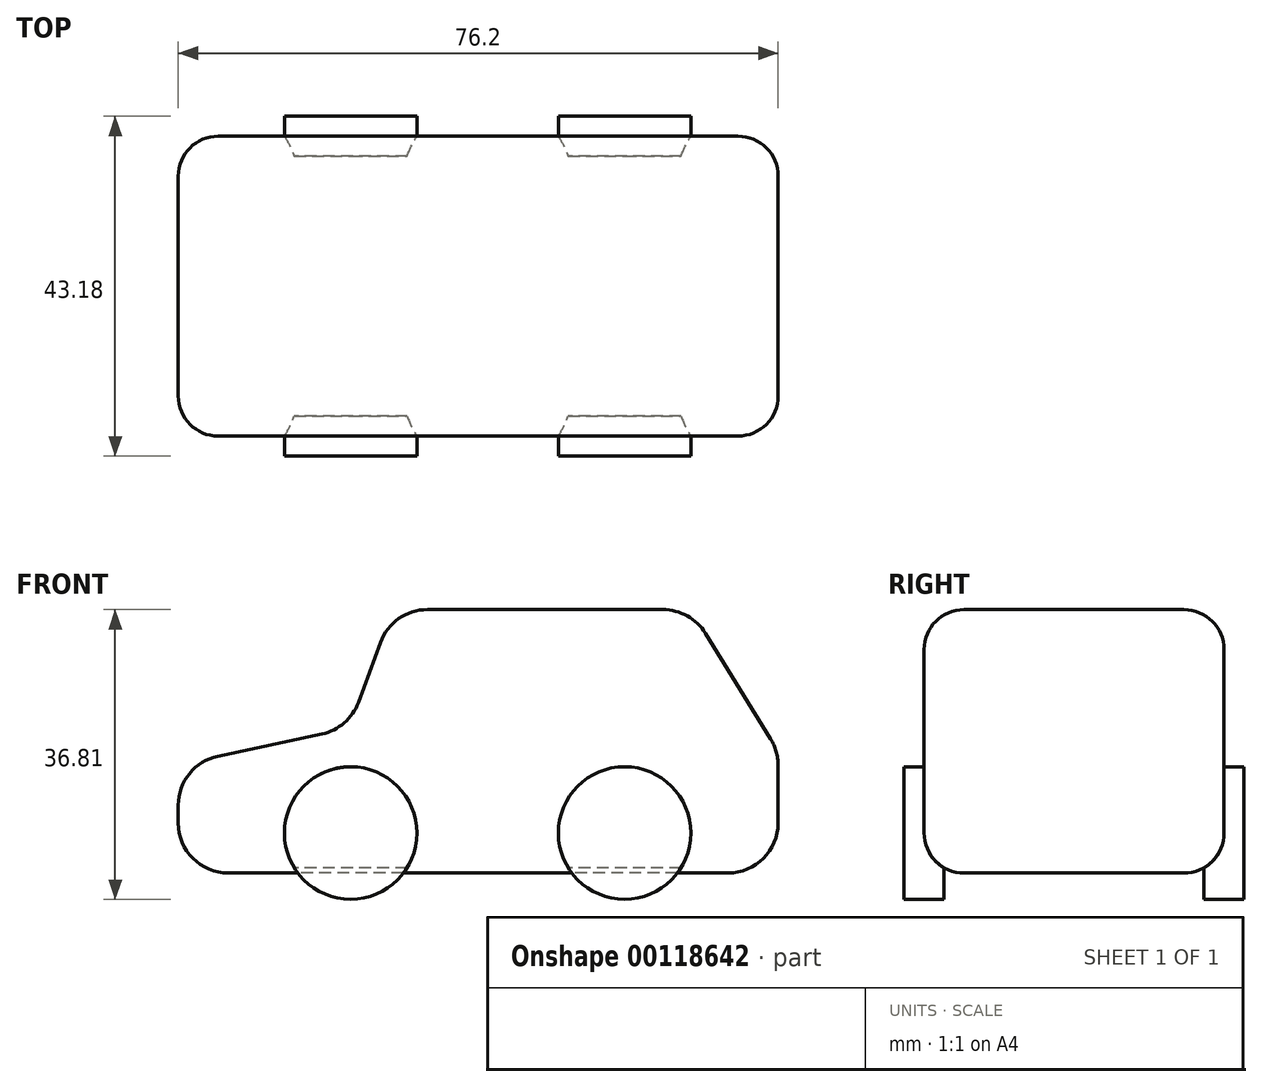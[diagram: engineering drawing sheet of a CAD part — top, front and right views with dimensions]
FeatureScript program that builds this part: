
annotation { "Feature Type Name" : "Feature", "Feature Type Description" : "" }
export const myFeature = defineFeature(function(context is Context, id is Id, definition is map)
    precondition{}
    {
        {
            var Q0;
            Q0=qCreatedBy(makeId("Front.planeOp"),FACE);
            var sketch = newSketch(context, id + "F0", { "sketchPlane" : qUnion([Q0])});
            skLineSegment(sketch, "E0", {"start": v(-45.02, 25.7) * mm, "end": v(-31.8, 28.52) * mm});
            skLineSegment(sketch, "E1", {"start": v(-27.16, 32.54) * mm, "end": v(-24.36, 40.17) * mm});
            skLineSegment(sketch, "E2", {"start": v(-18.4, 44.33) * mm, "end": v(11.53, 44.33) * mm});
            skLineSegment(sketch, "E3", {"start": v(16.93, 41.31) * mm, "end": v(25.2, 27.9) * mm});
            skLineSegment(sketch, "E4", {"start": v(26.15, 24.57) * mm, "end": v(26.15, 17.2) * mm});
            skLineSegment(sketch, "E5", {"start": v(19.8, 10.86) * mm, "end": v(-43.7, 10.86) * mm});
            skLineSegment(sketch, "E6", {"start": v(-50.05, 17.2) * mm, "end": v(-50.05, 19.5) * mm});
            skPoint(sketch, "E7.visualSharp", {"position": v(-28.37, 29.26) * mm});
            skArc(sketch, "E7.filletArc", {"start": v(-31.8, 28.52) * mm, "mid": v(-28.96, 29.94) * mm, "end": v(-27.16, 32.54) * mm});
            skPoint(sketch, "E8.visualSharp", {"position": v(-22.83, 44.33) * mm});
            skArc(sketch, "E8.filletArc", {"start": v(-18.4, 44.33) * mm, "mid": v(-22.03, 43.18) * mm, "end": v(-24.36, 40.17) * mm});
            skPoint(sketch, "E9.visualSharp", {"position": v(15.07, 44.33) * mm});
            skArc(sketch, "E9.filletArc", {"start": v(16.93, 41.31) * mm, "mid": v(14.62, 43.52) * mm, "end": v(11.53, 44.33) * mm});
            skPoint(sketch, "E10.visualSharp", {"position": v(26.15, 26.37) * mm});
            skArc(sketch, "E10.filletArc", {"start": v(26.15, 24.57) * mm, "mid": v(25.91, 26.3) * mm, "end": v(25.2, 27.9) * mm});
            skPoint(sketch, "E11.visualSharp", {"position": v(26.15, 10.86) * mm});
            skArc(sketch, "E11.filletArc", {"start": v(19.8, 10.86) * mm, "mid": v(24.3, 12.72) * mm, "end": v(26.15, 17.2) * mm});
            skPoint(sketch, "E12.visualSharp", {"position": v(-50.05, 10.86) * mm});
            skArc(sketch, "E12.filletArc", {"start": v(-50.05, 17.2) * mm, "mid": v(-48.19, 12.72) * mm, "end": v(-43.7, 10.86) * mm});
            skPoint(sketch, "E13.visualSharp", {"position": v(-50.05, 24.63) * mm});
            skArc(sketch, "E13.filletArc", {"start": v(-45.02, 25.7) * mm, "mid": v(-48.63, 23.48) * mm, "end": v(-50.05, 19.5) * mm});
            skSolve(sketch);
        }
        {
            var Q0;
            Q0 = qSketchRegion(id + "F0", true);
            extrude(context, id + "F1", {"entities" : qUnion([Q0]), "endBound" : BoundingType.SYMMETRIC, "depth" : 38.1 * mm});
        }
        {
            var Q0;
            Q0=makeQuery(id+"F1.opExtrude","CAP_EDGE",EDGE,{"disambiguationData":[OSD([sQuery(id+"F0.wireOp",EDGE,"E2")])],"isStart":false});
            var Q1;
            Q1=makeQuery(id+"F1.opExtrude","CAP_EDGE",EDGE,{"disambiguationData":[OSD([sQuery(id+"F0.wireOp",EDGE,"E2")])],"isStart":true});
            fillet(context, id + "F2", {"entities" : qUnion([Q0, Q1]), "radius" : 5.08 * mm, "tangentPropagation" : true, "allowEdgeOverflow" : false});
        }
        {
            var Q0;
            Q0=makeQuery(id+"F1.opExtrude","CAP_FACE",FACE,{"disambiguationData":[OSD([sQuery(id+"F0.wireOp",EDGE,"E0"),sQuery(id+"F0.wireOp",EDGE,"E1"),sQuery(id+"F0.wireOp",EDGE,"E2"),sQuery(id+"F0.wireOp",EDGE,"E3"),sQuery(id+"F0.wireOp",EDGE,"E4"),sQuery(id+"F0.wireOp",EDGE,"E5"),sQuery(id+"F0.wireOp",EDGE,"E6"),sQuery(id+"F0.wireOp",EDGE,"E7.filletArc"),sQuery(id+"F0.wireOp",EDGE,"E8.filletArc"),sQuery(id+"F0.wireOp",EDGE,"E9.filletArc"),sQuery(id+"F0.wireOp",EDGE,"E10.filletArc"),sQuery(id+"F0.wireOp",EDGE,"E11.filletArc"),sQuery(id+"F0.wireOp",EDGE,"E12.filletArc"),sQuery(id+"F0.wireOp",EDGE,"E13.filletArc")])],"isStart":false});
            var sketch = newSketch(context, id + "F3", { "sketchPlane" : qUnion([Q0])});
            skCircle(sketch, "E14", {"center": v(-28.15, 15.94) * mm, "radius": 8.42 * mm});
            skCircle(sketch, "E15", {"center": v(6.65, 15.94) * mm, "radius": 8.42 * mm});
            skSolve(sketch);
        }
        {
            var Q0;
            {var subQ0=sQuery(id+"F3.wireOp",EDGE,"E15");var subQ1=sQuery(id+"F0.wireOp",EDGE,"E5");var subQ2=makeQuery(id+"F2.opFillet","BLEND_EDGE",EDGE,{"blendedFrom":[makeQuery(id+"F1.opExtrude","CAP_EDGE",EDGE,{"disambiguationData":[OSD([subQ1])],"isStart":false}),makeQuery(id+"F1.opExtrude","CAP_FACE",FACE,{"disambiguationData":[OSD([sQuery(id+"F0.wireOp",EDGE,"E0"),sQuery(id+"F0.wireOp",EDGE,"E1"),sQuery(id+"F0.wireOp",EDGE,"E2"),sQuery(id+"F0.wireOp",EDGE,"E3"),sQuery(id+"F0.wireOp",EDGE,"E4"),subQ1,sQuery(id+"F0.wireOp",EDGE,"E6"),sQuery(id+"F0.wireOp",EDGE,"E7.filletArc"),sQuery(id+"F0.wireOp",EDGE,"E8.filletArc"),sQuery(id+"F0.wireOp",EDGE,"E9.filletArc"),sQuery(id+"F0.wireOp",EDGE,"E10.filletArc"),sQuery(id+"F0.wireOp",EDGE,"E11.filletArc"),sQuery(id+"F0.wireOp",EDGE,"E12.filletArc"),sQuery(id+"F0.wireOp",EDGE,"E13.filletArc")])],"isStart":false})],"blendedInto":[makeQuery(id+"F1.opExtrude","CAP_FACE",FACE,{"disambiguationData":[OSD([sQuery(id+"F0.wireOp",EDGE,"E0"),sQuery(id+"F0.wireOp",EDGE,"E1"),sQuery(id+"F0.wireOp",EDGE,"E2"),sQuery(id+"F0.wireOp",EDGE,"E3"),sQuery(id+"F0.wireOp",EDGE,"E4"),subQ1,sQuery(id+"F0.wireOp",EDGE,"E6"),sQuery(id+"F0.wireOp",EDGE,"E7.filletArc"),sQuery(id+"F0.wireOp",EDGE,"E8.filletArc"),sQuery(id+"F0.wireOp",EDGE,"E9.filletArc"),sQuery(id+"F0.wireOp",EDGE,"E10.filletArc"),sQuery(id+"F0.wireOp",EDGE,"E11.filletArc"),sQuery(id+"F0.wireOp",EDGE,"E12.filletArc"),sQuery(id+"F0.wireOp",EDGE,"E13.filletArc")])],"isStart":false})]});var subQ3=makeQuery(id+"F3.imprint","INTERSECT",VERTEX,{"disambiguationData":[OD(0.0)],"derivedFrom":[subQ2,subQ0]});Q0=makeQuery(id+"F3.imprint","IMPRINT",FACE,{"disambiguationData":[TD([[makeQuery(id+"F3.imprint","IMPRINT",EDGE,{"disambiguationData":[TD([[subQ3,1.0]])],"derivedFrom":subQ0}),1.0]])]});}
            var Q1;
            {var subQ0=sQuery(id+"F3.wireOp",EDGE,"E15");var subQ1=sQuery(id+"F0.wireOp",EDGE,"E5");var subQ2=makeQuery(id+"F2.opFillet","BLEND_EDGE",EDGE,{"blendedFrom":[makeQuery(id+"F1.opExtrude","CAP_EDGE",EDGE,{"disambiguationData":[OSD([subQ1])],"isStart":false}),makeQuery(id+"F1.opExtrude","CAP_FACE",FACE,{"disambiguationData":[OSD([sQuery(id+"F0.wireOp",EDGE,"E0"),sQuery(id+"F0.wireOp",EDGE,"E1"),sQuery(id+"F0.wireOp",EDGE,"E2"),sQuery(id+"F0.wireOp",EDGE,"E3"),sQuery(id+"F0.wireOp",EDGE,"E4"),subQ1,sQuery(id+"F0.wireOp",EDGE,"E6"),sQuery(id+"F0.wireOp",EDGE,"E7.filletArc"),sQuery(id+"F0.wireOp",EDGE,"E8.filletArc"),sQuery(id+"F0.wireOp",EDGE,"E9.filletArc"),sQuery(id+"F0.wireOp",EDGE,"E10.filletArc"),sQuery(id+"F0.wireOp",EDGE,"E11.filletArc"),sQuery(id+"F0.wireOp",EDGE,"E12.filletArc"),sQuery(id+"F0.wireOp",EDGE,"E13.filletArc")])],"isStart":false})],"blendedInto":[makeQuery(id+"F1.opExtrude","CAP_FACE",FACE,{"disambiguationData":[OSD([sQuery(id+"F0.wireOp",EDGE,"E0"),sQuery(id+"F0.wireOp",EDGE,"E1"),sQuery(id+"F0.wireOp",EDGE,"E2"),sQuery(id+"F0.wireOp",EDGE,"E3"),sQuery(id+"F0.wireOp",EDGE,"E4"),subQ1,sQuery(id+"F0.wireOp",EDGE,"E6"),sQuery(id+"F0.wireOp",EDGE,"E7.filletArc"),sQuery(id+"F0.wireOp",EDGE,"E8.filletArc"),sQuery(id+"F0.wireOp",EDGE,"E9.filletArc"),sQuery(id+"F0.wireOp",EDGE,"E10.filletArc"),sQuery(id+"F0.wireOp",EDGE,"E11.filletArc"),sQuery(id+"F0.wireOp",EDGE,"E12.filletArc"),sQuery(id+"F0.wireOp",EDGE,"E13.filletArc")])],"isStart":false})]});var subQ3=makeQuery(id+"F3.imprint","INTERSECT",VERTEX,{"disambiguationData":[OD(0.0)],"derivedFrom":[subQ2,subQ0]});Q1=makeQuery(id+"F3.imprint","IMPRINT",FACE,{"disambiguationData":[TD([[makeQuery(id+"F3.imprint","IMPRINT",EDGE,{"disambiguationData":[TD([[subQ3,-1.0]])],"derivedFrom":subQ0}),1.0]])]});}
            var Q2;
            {var subQ0=sQuery(id+"F3.wireOp",EDGE,"E14");var subQ1=sQuery(id+"F0.wireOp",EDGE,"E7.filletArc");var subQ2=sQuery(id+"F0.wireOp",EDGE,"E0");var subQ3=makeQuery(id+"F1.opExtrude","CAP_FACE",FACE,{"disambiguationData":[OSD([subQ2,sQuery(id+"F0.wireOp",EDGE,"E1"),sQuery(id+"F0.wireOp",EDGE,"E2"),sQuery(id+"F0.wireOp",EDGE,"E3"),sQuery(id+"F0.wireOp",EDGE,"E4"),sQuery(id+"F0.wireOp",EDGE,"E5"),sQuery(id+"F0.wireOp",EDGE,"E6"),subQ1,sQuery(id+"F0.wireOp",EDGE,"E8.filletArc"),sQuery(id+"F0.wireOp",EDGE,"E9.filletArc"),sQuery(id+"F0.wireOp",EDGE,"E10.filletArc"),sQuery(id+"F0.wireOp",EDGE,"E11.filletArc"),sQuery(id+"F0.wireOp",EDGE,"E12.filletArc"),sQuery(id+"F0.wireOp",EDGE,"E13.filletArc")])],"isStart":false});var subQ4=makeQuery(id+"F2.opFillet","BLEND_EDGE",EDGE,{"blendedFrom":[makeQuery(id+"F1.opExtrude","CAP_EDGE",EDGE,{"disambiguationData":[OSD([subQ1])],"isStart":false}),subQ3],"blendedInto":[subQ3]});var subQ5=makeQuery(id+"F3.imprint","INTERSECT",VERTEX,{"derivedFrom":[subQ4,subQ0]});Q2=makeQuery(id+"F3.imprint","IMPRINT",FACE,{"disambiguationData":[TD([[makeQuery(id+"F3.imprint","IMPRINT",EDGE,{"disambiguationData":[TD([[subQ5,-1.0]])],"derivedFrom":subQ0}),1.0]])]});}
            var Q3;
            {var subQ0=sQuery(id+"F0.wireOp",EDGE,"E7.filletArc");var subQ1=sQuery(id+"F0.wireOp",EDGE,"E5");var subQ2=sQuery(id+"F0.wireOp",EDGE,"E0");var subQ3=makeQuery(id+"F1.opExtrude","CAP_FACE",FACE,{"disambiguationData":[OSD([subQ2,sQuery(id+"F0.wireOp",EDGE,"E1"),sQuery(id+"F0.wireOp",EDGE,"E2"),sQuery(id+"F0.wireOp",EDGE,"E3"),sQuery(id+"F0.wireOp",EDGE,"E4"),subQ1,sQuery(id+"F0.wireOp",EDGE,"E6"),subQ0,sQuery(id+"F0.wireOp",EDGE,"E8.filletArc"),sQuery(id+"F0.wireOp",EDGE,"E9.filletArc"),sQuery(id+"F0.wireOp",EDGE,"E10.filletArc"),sQuery(id+"F0.wireOp",EDGE,"E11.filletArc"),sQuery(id+"F0.wireOp",EDGE,"E12.filletArc"),sQuery(id+"F0.wireOp",EDGE,"E13.filletArc")])],"isStart":false});var subQ4=makeQuery(id+"F2.opFillet","BLEND_EDGE",EDGE,{"blendedFrom":[makeQuery(id+"F1.opExtrude","CAP_EDGE",EDGE,{"disambiguationData":[OSD([subQ0])],"isStart":false}),subQ3],"blendedInto":[subQ3]});var subQ7=sQuery(id+"F3.wireOp",EDGE,"E14");var subQ8=makeQuery(id+"F3.imprint","INTERSECT",VERTEX,{"derivedFrom":[subQ4,subQ7]});Q3=makeQuery(id+"F3.imprint","IMPRINT",FACE,{"disambiguationData":[TD([[makeQuery(id+"F3.imprint","IMPRINT",EDGE,{"disambiguationData":[TD([[subQ8,1.0]])],"derivedFrom":subQ7}),1.0]])]});}
            var Q4;
            {var subQ0=sQuery(id+"F3.wireOp",EDGE,"E14");var subQ1=sQuery(id+"F0.wireOp",EDGE,"E5");var subQ2=makeQuery(id+"F2.opFillet","BLEND_EDGE",EDGE,{"blendedFrom":[makeQuery(id+"F1.opExtrude","CAP_EDGE",EDGE,{"disambiguationData":[OSD([subQ1])],"isStart":false}),makeQuery(id+"F1.opExtrude","CAP_FACE",FACE,{"disambiguationData":[OSD([sQuery(id+"F0.wireOp",EDGE,"E0"),sQuery(id+"F0.wireOp",EDGE,"E1"),sQuery(id+"F0.wireOp",EDGE,"E2"),sQuery(id+"F0.wireOp",EDGE,"E3"),sQuery(id+"F0.wireOp",EDGE,"E4"),subQ1,sQuery(id+"F0.wireOp",EDGE,"E6"),sQuery(id+"F0.wireOp",EDGE,"E7.filletArc"),sQuery(id+"F0.wireOp",EDGE,"E8.filletArc"),sQuery(id+"F0.wireOp",EDGE,"E9.filletArc"),sQuery(id+"F0.wireOp",EDGE,"E10.filletArc"),sQuery(id+"F0.wireOp",EDGE,"E11.filletArc"),sQuery(id+"F0.wireOp",EDGE,"E12.filletArc"),sQuery(id+"F0.wireOp",EDGE,"E13.filletArc")])],"isStart":false})],"blendedInto":[makeQuery(id+"F1.opExtrude","CAP_FACE",FACE,{"disambiguationData":[OSD([sQuery(id+"F0.wireOp",EDGE,"E0"),sQuery(id+"F0.wireOp",EDGE,"E1"),sQuery(id+"F0.wireOp",EDGE,"E2"),sQuery(id+"F0.wireOp",EDGE,"E3"),sQuery(id+"F0.wireOp",EDGE,"E4"),subQ1,sQuery(id+"F0.wireOp",EDGE,"E6"),sQuery(id+"F0.wireOp",EDGE,"E7.filletArc"),sQuery(id+"F0.wireOp",EDGE,"E8.filletArc"),sQuery(id+"F0.wireOp",EDGE,"E9.filletArc"),sQuery(id+"F0.wireOp",EDGE,"E10.filletArc"),sQuery(id+"F0.wireOp",EDGE,"E11.filletArc"),sQuery(id+"F0.wireOp",EDGE,"E12.filletArc"),sQuery(id+"F0.wireOp",EDGE,"E13.filletArc")])],"isStart":false})]});var subQ3=makeQuery(id+"F3.imprint","INTERSECT",VERTEX,{"disambiguationData":[OD(0.0)],"derivedFrom":[subQ2,subQ0]});Q4=makeQuery(id+"F3.imprint","IMPRINT",FACE,{"disambiguationData":[TD([[makeQuery(id+"F3.imprint","IMPRINT",EDGE,{"disambiguationData":[TD([[subQ3,1.0]])],"derivedFrom":subQ0}),1.0]])]});}
            extrude(context, id + "F4", {"entities" : qUnion([Q0, Q1, Q2, Q3, Q4]), "operationType" : NewBodyOperationType.ADD, "endBound" : BoundingType.SYMMETRIC, "oppositeDirection" : true, "depth" : 5.08 * mm});
        }
        {
            var Q0;
            Q0=makeQuery(id+"F1.opExtrude","SWEPT_BODY",BODY,{"disambiguationData":[OSD([sQuery(id+"F0.wireOp",EDGE,"E0"),sQuery(id+"F0.wireOp",EDGE,"E1"),sQuery(id+"F0.wireOp",EDGE,"E2"),sQuery(id+"F0.wireOp",EDGE,"E3"),sQuery(id+"F0.wireOp",EDGE,"E4"),sQuery(id+"F0.wireOp",EDGE,"E5"),sQuery(id+"F0.wireOp",EDGE,"E6"),sQuery(id+"F0.wireOp",EDGE,"E7.filletArc"),sQuery(id+"F0.wireOp",EDGE,"E8.filletArc"),sQuery(id+"F0.wireOp",EDGE,"E9.filletArc"),sQuery(id+"F0.wireOp",EDGE,"E10.filletArc"),sQuery(id+"F0.wireOp",EDGE,"E11.filletArc"),sQuery(id+"F0.wireOp",EDGE,"E12.filletArc"),sQuery(id+"F0.wireOp",EDGE,"E13.filletArc")])]});
            var Q1;
            Q1=qCreatedBy(makeId("Front.planeOp"),FACE);
            mirror(context, id + "F5", {"operationType" : NewBodyOperationType.ADD, "entities" : qUnion([Q0]), "mirrorPlane" : qUnion([Q1])});
        }
    });
